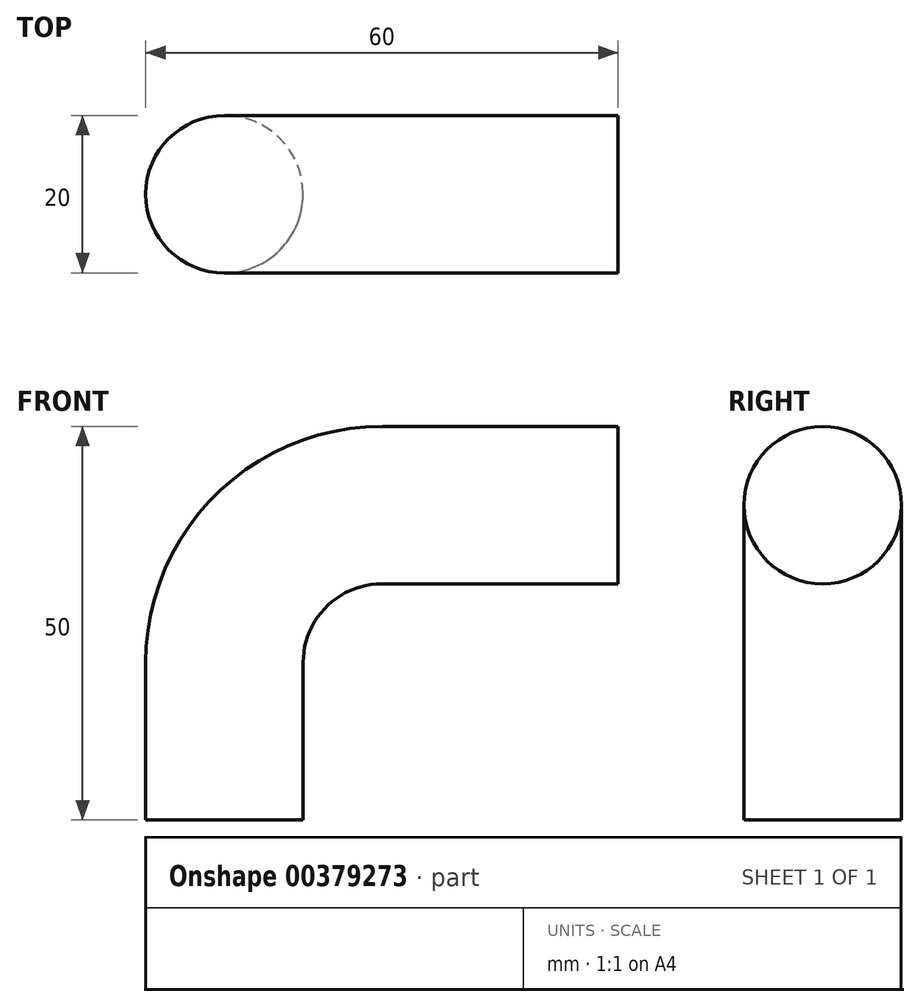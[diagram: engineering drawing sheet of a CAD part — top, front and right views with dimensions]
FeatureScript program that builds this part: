
annotation { "Feature Type Name" : "Feature", "Feature Type Description" : "" }
export const myFeature = defineFeature(function(context is Context, id is Id, definition is map)
    precondition{}
    {
        {
            var Q0;
            Q0=qCreatedBy(makeId("Front.planeOp"),FACE);
            var sketch = newSketch(context, id + "F0", { "sketchPlane" : qUnion([Q0])});
            skLineSegment(sketch, "E0", {"start": v(0, 0) * mm, "end": v(0, 20) * mm});
            skLineSegment(sketch, "E1", {"start": v(20, 40) * mm, "end": v(50, 40) * mm});
            skPoint(sketch, "E2.visualSharp", {"position": v(0, 40) * mm});
            skArc(sketch, "E2.filletArc", {"start": v(20, 40) * mm, "mid": v(5.86, 34.14) * mm, "end": v(0, 20) * mm});
            skSolve(sketch);
        }
        {
            var Q0;
            Q0=qCreatedBy(makeId("Top.planeOp"),FACE);
            var sketch = newSketch(context, id + "F1", { "sketchPlane" : qUnion([Q0])});
            skCircle(sketch, "E3", {"center": v(0, 0) * mm, "radius": 10 * mm});
            skSolve(sketch);
        }
        {
            var Q0;
            Q0=makeQuery(id+"F1.imprint","IMPRINT",FACE,{"disambiguationData":[TD([[makeQuery(id+"F1.imprint","IMPRINT",EDGE,{"derivedFrom":sQuery(id+"F1.wireOp",EDGE,"E3")}),1.0]])]});
            var Q1;
            Q1=sQuery(id+"F0.wireOp",EDGE,"E0");
            var Q2;
            Q2=sQuery(id+"F0.wireOp",EDGE,"E2.filletArc");
            var Q3;
            Q3=sQuery(id+"F0.wireOp",EDGE,"E1");
            sweep(context, id + "F2", {"profiles" : qUnion([Q0]), "path" : qUnion([Q1, Q2, Q3])});
        }
        {
            var Q0;
            Q0=makeQuery(id+"F2.opSweep","SWEPT_BODY",BODY,{"disambiguationData":[OSD([sQuery(id+"F0.wireOp",EDGE,"E1"),sQuery(id+"F1.wireOp",EDGE,"E3")])]});
            transform(context, id + "F3", {"entities" : qUnion([Q0]), "transformType" : TransformType.TRANSLATION_3D, "dx" : 0 * mm, "dy" : 0 * mm, "dz" : 0 * mm, "makeCopy" : true});
        }
    });
